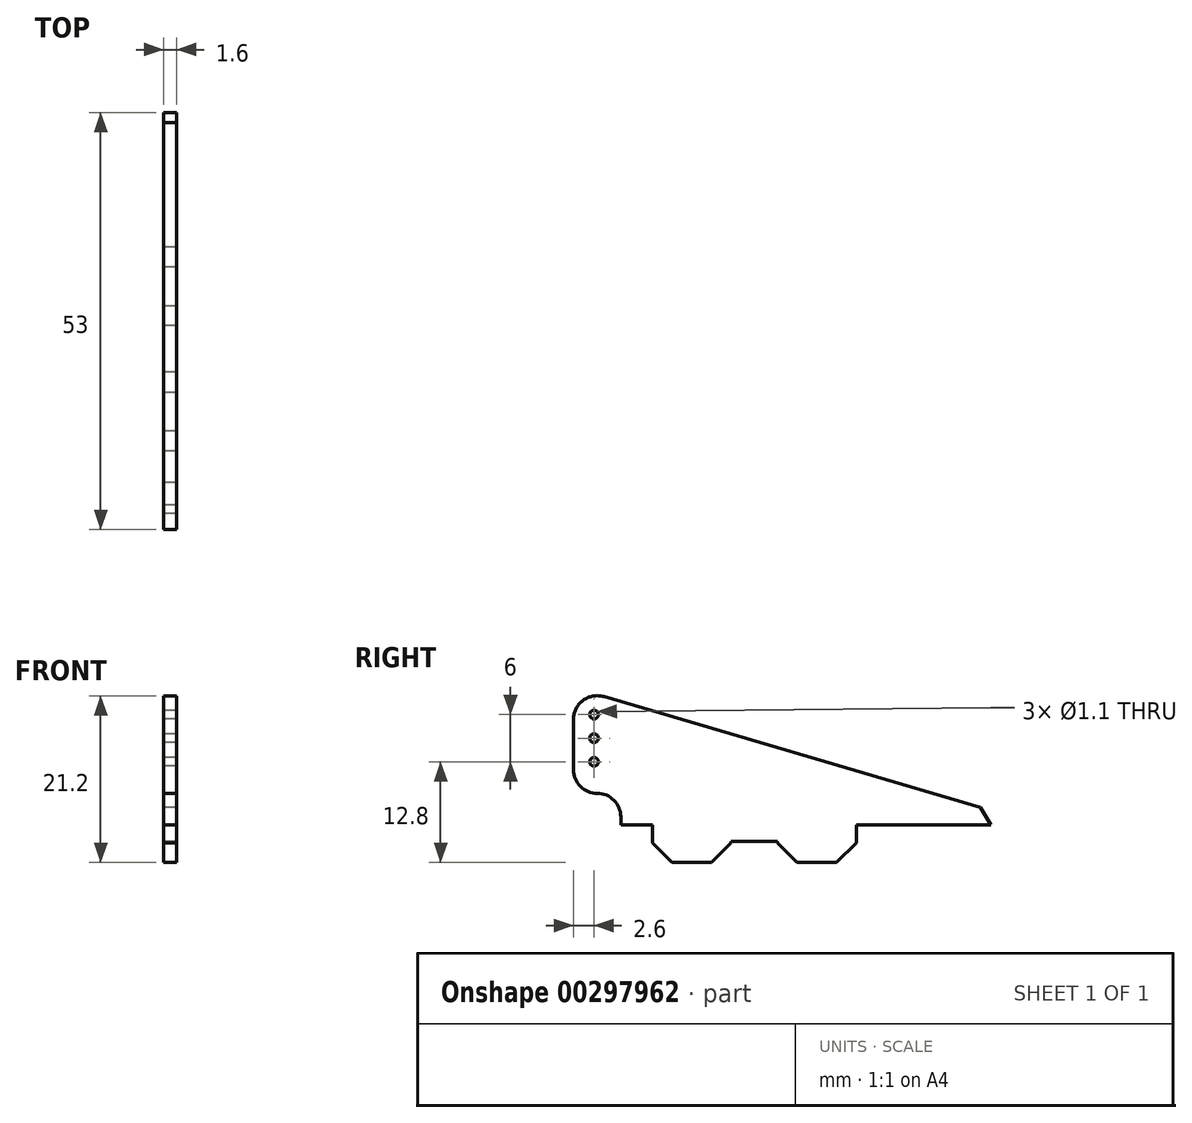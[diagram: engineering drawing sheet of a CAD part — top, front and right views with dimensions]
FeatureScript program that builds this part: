
annotation { "Feature Type Name" : "Feature", "Feature Type Description" : "" }
export const myFeature = defineFeature(function(context is Context, id is Id, definition is map)
    precondition{}
    {
        {
            var Q0;
            Q0=qCreatedBy(makeId("Right.planeOp"),FACE);
            var sketch = newSketch(context, id + "F0", { "sketchPlane" : qUnion([Q0])});
            skLineSegment(sketch, "E0", {"start": v(3.4, 0) * mm, "end": v(7.4, 0) * mm});
            skLineSegment(sketch, "E1", {"start": v(7.4, 0) * mm, "end": v(7.4, -4.8) * mm});
            skLineSegment(sketch, "E2", {"start": v(7.4, -4.8) * mm, "end": v(17.4, -4.8) * mm});
            skLineSegment(sketch, "E3", {"start": v(17.4, -4.8) * mm, "end": v(17.4, -2.1) * mm});
            skLineSegment(sketch, "E4", {"start": v(17.4, -2.1) * mm, "end": v(23.3, -2.1) * mm});
            skLineSegment(sketch, "E5", {"start": v(23.3, -2.1) * mm, "end": v(23.3, -4.8) * mm});
            skLineSegment(sketch, "E6", {"start": v(23.3, -4.8) * mm, "end": v(33.3, -4.8) * mm});
            skLineSegment(sketch, "E7", {"start": v(33.3, -4.8) * mm, "end": v(33.3, 0) * mm});
            skLineSegment(sketch, "E8", {"start": v(33.3, 0) * mm, "end": v(50.4, 0) * mm});
            skLineSegment(sketch, "E9", {"start": v(50.4, 0) * mm, "end": v(49.1, 2.2) * mm});
            skLineSegment(sketch, "E10", {"start": v(49.1, 2.2) * mm, "end": v(1.25, 16.28) * mm});
            skArc(sketch, "E11", {"start": v(1.25, 16.28) * mm, "mid": v(-1.4, 15.8) * mm, "end": v(-2.6, 13.4) * mm});
            skLineSegment(sketch, "E12", {"start": v(-2.6, 13.4) * mm, "end": v(-2.6, 7) * mm});
            skArc(sketch, "E13", {"start": v(-2.6, 7) * mm, "mid": v(-1.72, 4.88) * mm, "end": v(0.4, 4) * mm});
            skLineSegment(sketch, "E14", {"start": v(0.4, 4) * mm, "end": v(0.4, 4) * mm});
            skArc(sketch, "E15", {"start": v(0.4, 4) * mm, "mid": v(2.52, 3.12) * mm, "end": v(3.4, 1) * mm});
            skLineSegment(sketch, "E16", {"start": v(3.4, 1) * mm, "end": v(3.4, 0) * mm});
            skSolve(sketch);
        }
        {
            var Q0;
            Q0=makeQuery(id+"F0.imprint","IMPRINT",FACE,{"disambiguationData":[TD([[makeQuery(id+"F0.imprint","IMPRINT",EDGE,{"derivedFrom":sQuery(id+"F0.wireOp",EDGE,"E0")}),1.0]])]});
            extrude(context, id + "F1", {"entities" : qUnion([Q0]), "depth" : 1.6 * mm, "symmetric" : true});
        }
        {
            var Q0;
            Q0=makeQuery(id+"F1.opExtrude","SWEPT_EDGE",EDGE,{"disambiguationData":[OSD([sQuery(id+"F0.wireOp",EDGE,"E1"),sQuery(id+"F0.wireOp",EDGE,"E2")])]});
            var Q1;
            Q1=makeQuery(id+"F1.opExtrude","SWEPT_EDGE",EDGE,{"disambiguationData":[OSD([sQuery(id+"F0.wireOp",EDGE,"E5"),sQuery(id+"F0.wireOp",EDGE,"E6")])]});
            var Q2;
            Q2=makeQuery(id+"F1.opExtrude","SWEPT_EDGE",EDGE,{"disambiguationData":[OSD([sQuery(id+"F0.wireOp",EDGE,"E2"),sQuery(id+"F0.wireOp",EDGE,"E3")])]});
            var Q3;
            Q3=makeQuery(id+"F1.opExtrude","SWEPT_EDGE",EDGE,{"disambiguationData":[OSD([sQuery(id+"F0.wireOp",EDGE,"E6"),sQuery(id+"F0.wireOp",EDGE,"E7")])]});
            chamfer(context, id + "F2", {"entities" : qUnion([Q0, Q1, Q2, Q3]), "width" : 2.5 * mm, "tangentPropagation" : true});
        }
        {
            var Q0;
            Q0=makeQuery(id+"F1.opExtrude","CAP_FACE",FACE,{"disambiguationData":[OSD([sQuery(id+"F0.wireOp",EDGE,"E0"),sQuery(id+"F0.wireOp",EDGE,"E1"),sQuery(id+"F0.wireOp",EDGE,"E2"),sQuery(id+"F0.wireOp",EDGE,"E3"),sQuery(id+"F0.wireOp",EDGE,"E4"),sQuery(id+"F0.wireOp",EDGE,"E5"),sQuery(id+"F0.wireOp",EDGE,"E6"),sQuery(id+"F0.wireOp",EDGE,"E7"),sQuery(id+"F0.wireOp",EDGE,"E8"),sQuery(id+"F0.wireOp",EDGE,"E9"),sQuery(id+"F0.wireOp",EDGE,"E10"),sQuery(id+"F0.wireOp",EDGE,"E11"),sQuery(id+"F0.wireOp",EDGE,"E12"),sQuery(id+"F0.wireOp",EDGE,"E13"),sQuery(id+"F0.wireOp",EDGE,"E15"),sQuery(id+"F0.wireOp",EDGE,"E16")])],"isStart":false});
            var sketch = newSketch(context, id + "F3", { "sketchPlane" : qUnion([Q0])});
            skLineSegment(sketch, "E17", {"start": v(0, 14) * mm, "end": v(0, 11) * mm, "construction": true});
            skLineSegment(sketch, "E18", {"start": v(0, 11) * mm, "end": v(0, 8) * mm, "construction": true});
            skSolve(sketch);
        }
        {
            var Q0;
            Q0=sQuery(id+"F3.wireOp",VERTEX,"E17.start");
            var Q1;
            Q1=sQuery(id+"F3.wireOp",VERTEX,"E17.end");
            var Q2;
            Q2=sQuery(id+"F3.wireOp",VERTEX,"E18.end");
            var Q3;
            Q3=makeQuery(id+"F1.opExtrude","SWEPT_BODY",BODY,{"disambiguationData":[OSD([sQuery(id+"F0.wireOp",EDGE,"E0"),sQuery(id+"F0.wireOp",EDGE,"E1"),sQuery(id+"F0.wireOp",EDGE,"E2"),sQuery(id+"F0.wireOp",EDGE,"E3"),sQuery(id+"F0.wireOp",EDGE,"E4"),sQuery(id+"F0.wireOp",EDGE,"E5"),sQuery(id+"F0.wireOp",EDGE,"E6"),sQuery(id+"F0.wireOp",EDGE,"E7"),sQuery(id+"F0.wireOp",EDGE,"E8"),sQuery(id+"F0.wireOp",EDGE,"E9"),sQuery(id+"F0.wireOp",EDGE,"E10"),sQuery(id+"F0.wireOp",EDGE,"E11"),sQuery(id+"F0.wireOp",EDGE,"E12"),sQuery(id+"F0.wireOp",EDGE,"E13"),sQuery(id+"F0.wireOp",EDGE,"E15"),sQuery(id+"F0.wireOp",EDGE,"E16")])]});
            hole(context, id + "F4", {"style" : HoleStyle.SIMPLE, "endStyle" : HoleEndStyle.THROUGH, "holeDiameter" : 1.1 * mm, "tappedDepth" : 12 * mm, "tapClearance" : 3, "locations" : qUnion([Q0, Q1, Q2]), "scope" : qUnion([Q3])});
        }
    });
